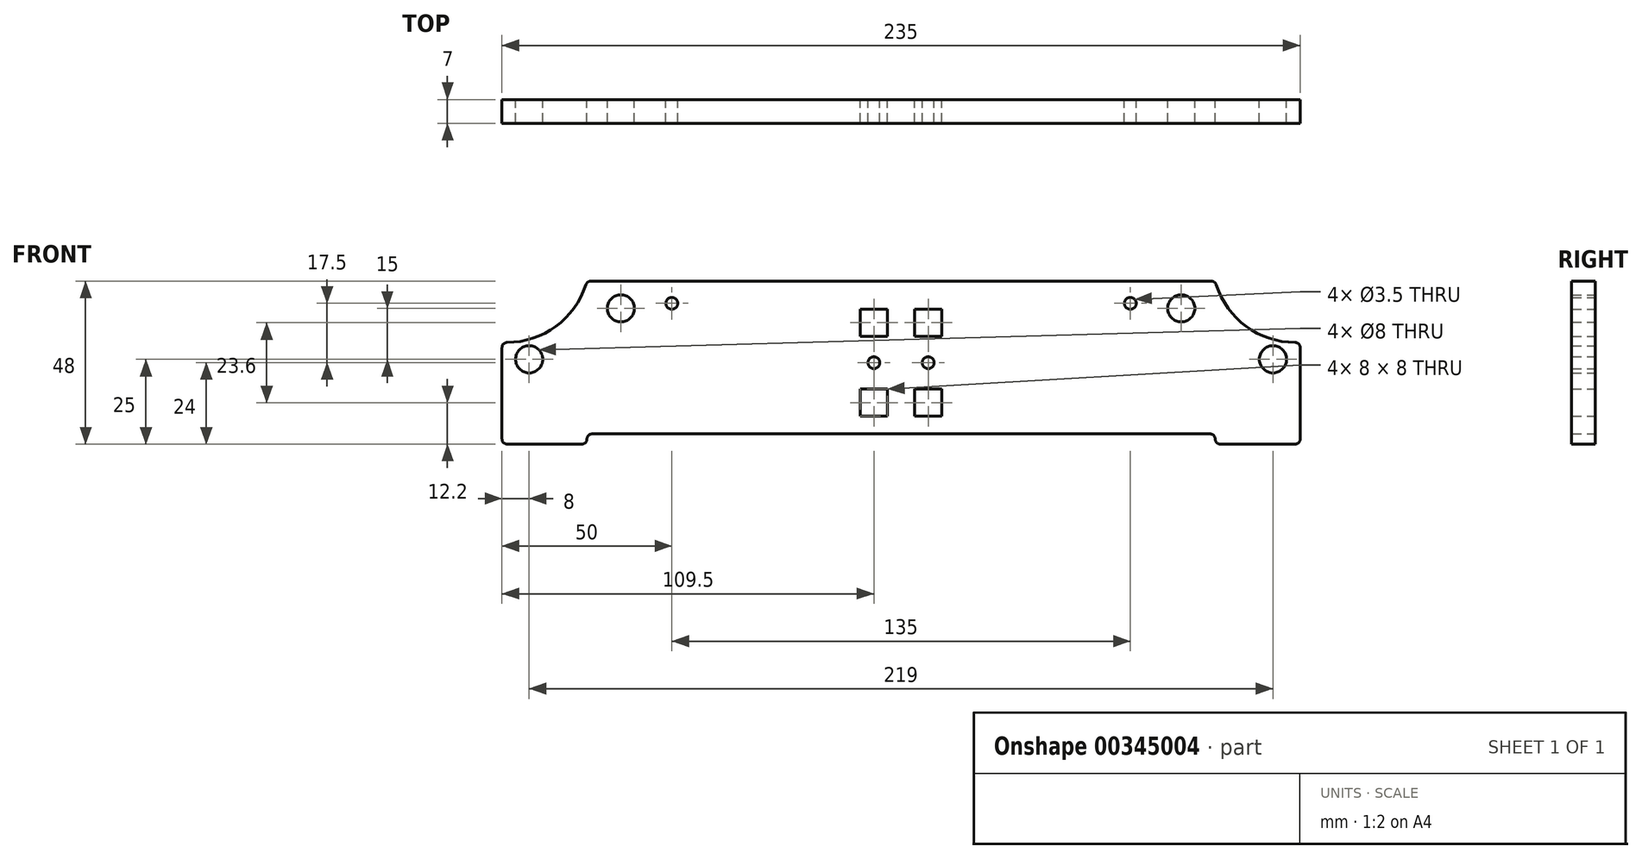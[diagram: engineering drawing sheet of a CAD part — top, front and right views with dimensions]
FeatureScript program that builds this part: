
annotation { "Feature Type Name" : "Feature", "Feature Type Description" : "" }
export const myFeature = defineFeature(function(context is Context, id is Id, definition is map)
    precondition{}
    {
        {
            var Q0;
            Q0=qCreatedBy(makeId("Front.planeOp"),FACE);
            var sketch = newSketch(context, id + "F0", { "sketchPlane" : qUnion([Q0])});
            skLineSegment(sketch, "E0", {"start": v(-117.5, 0) * mm, "end": v(117.5, 0) * mm, "construction": true});
            skLineSegment(sketch, "E1", {"start": v(0, 24) * mm, "end": v(0, -24) * mm, "construction": true});
            skPoint(sketch, "E2", {"position": v(-92.5, 0) * mm});
            skPoint(sketch, "E3.MirrorP", {"position": v(92.5, 0) * mm});
            skPoint(sketch, "E4", {"position": v(0, 21) * mm});
            skPoint(sketch, "E5.MirrorP", {"position": v(0, -21) * mm});
            skSolve(sketch);
        }
        {
            var Q0;
            Q0=qCreatedBy(makeId("Front.planeOp"),FACE);
            var sketch = newSketch(context, id + "F1", { "sketchPlane" : qUnion([Q0])});
            skLineSegment(sketch, "E6.0", {"start": v(-117.5, 0) * mm, "end": v(117.5, 0) * mm, "construction": true});
            skLineSegment(sketch, "E6.1", {"start": v(0, 24) * mm, "end": v(0, -24) * mm, "construction": true});
            skLineSegment(sketch, "E7", {"start": v(-91, -21) * mm, "end": v(92.5, -21) * mm});
            skLineSegment(sketch, "E8", {"start": v(-116, -24) * mm, "end": v(-94, -24) * mm});
            skLineSegment(sketch, "E9", {"start": v(-92.5, -22.5) * mm, "end": v(-92.5, -22.5) * mm});
            skPoint(sketch, "E10.visualSharp", {"position": v(-92.5, -24) * mm});
            skArc(sketch, "E10.filletArc", {"start": v(-94, -24) * mm, "mid": v(-92.94, -23.56) * mm, "end": v(-92.5, -22.5) * mm});
            skPoint(sketch, "E11.visualSharp", {"position": v(-92.5, -21) * mm});
            skArc(sketch, "E11.filletArc", {"start": v(-91, -21) * mm, "mid": v(-92.06, -21.44) * mm, "end": v(-92.5, -22.5) * mm});
            skArc(sketch, "E12.MirrorCS", {"start": v(-94, -24) * mm, "mid": v(-92.94, -24.44) * mm, "end": v(-92.5, -25.5) * mm});
            skArc(sketch, "E13.MirrorCS", {"start": v(-91, -27) * mm, "mid": v(-92.06, -26.56) * mm, "end": v(-92.5, -25.5) * mm});
            skPoint(sketch, "E14.MirrorP", {"position": v(-92.5, -27) * mm});
            skArc(sketch, "E15.MirrorCS", {"start": v(94, -24) * mm, "mid": v(92.94, -23.56) * mm, "end": v(92.5, -22.5) * mm});
            skArc(sketch, "E16.MirrorCS", {"start": v(94, -24) * mm, "mid": v(92.94, -24.44) * mm, "end": v(92.5, -25.5) * mm});
            skArc(sketch, "E17.MirrorCS", {"start": v(91, -21) * mm, "mid": v(92.06, -21.44) * mm, "end": v(92.5, -22.5) * mm});
            skArc(sketch, "E18.MirrorCS", {"start": v(91, -27) * mm, "mid": v(92.06, -26.56) * mm, "end": v(92.5, -25.5) * mm});
            skPoint(sketch, "E19.MirrorP", {"position": v(92.5, -24) * mm});
            skPoint(sketch, "E20.MirrorP", {"position": v(92.5, -21) * mm});
            skLineSegment(sketch, "E21.MirrorCS", {"start": v(92.5, -22.5) * mm, "end": v(92.5, -22.5) * mm});
            skPoint(sketch, "E22.MirrorP", {"position": v(92.5, -27) * mm});
            skLineSegment(sketch, "E23.MirrorCS", {"start": v(116, -24) * mm, "end": v(94, -24) * mm});
            skLineSegment(sketch, "E24", {"start": v(-91.38, 24) * mm, "end": v(92.5, 24) * mm});
            skLineSegment(sketch, "E25", {"start": v(-117.5, -22.5) * mm, "end": v(-117.5, 4.46) * mm});
            skLineSegment(sketch, "E26.MirrorCS", {"start": v(117.5, -22.5) * mm, "end": v(117.5, 6) * mm});
            skArc(sketch, "E27", {"start": v(-116, 5.96) * mm, "mid": v(-101.65, 10.7) * mm, "end": v(-92.8, 22.96) * mm});
            skPoint(sketch, "E28.visualSharp", {"position": v(-92.5, 24) * mm});
            skArc(sketch, "E28.filletArc", {"start": v(-91.38, 24) * mm, "mid": v(-92.26, 23.71) * mm, "end": v(-92.8, 22.96) * mm});
            skPoint(sketch, "E29.visualSharp", {"position": v(-117.5, 6) * mm});
            skArc(sketch, "E29.filletArc", {"start": v(-116, 5.96) * mm, "mid": v(-117.06, 5.52) * mm, "end": v(-117.5, 4.46) * mm});
            skArc(sketch, "E30.MirrorCS", {"start": v(116, 5.96) * mm, "mid": v(101.65, 10.7) * mm, "end": v(92.8, 22.96) * mm});
            skPoint(sketch, "E31.MirrorP", {"position": v(92.5, 24) * mm});
            skArc(sketch, "E32.MirrorCS", {"start": v(91.38, 24) * mm, "mid": v(92.26, 23.71) * mm, "end": v(92.8, 22.96) * mm});
            skArc(sketch, "E33.MirrorCS", {"start": v(116, 5.96) * mm, "mid": v(117.06, 5.52) * mm, "end": v(117.5, 4.46) * mm});
            skPoint(sketch, "E34.visualSharp", {"position": v(-117.5, -24) * mm});
            skArc(sketch, "E34.filletArc", {"start": v(-117.5, -22.5) * mm, "mid": v(-117.06, -23.56) * mm, "end": v(-116, -24) * mm});
            skPoint(sketch, "E35.visualSharp", {"position": v(117.5, -24) * mm});
            skArc(sketch, "E35.filletArc", {"start": v(116, -24) * mm, "mid": v(117.06, -23.56) * mm, "end": v(117.5, -22.5) * mm});
            skLineSegment(sketch, "E36.bottom", {"start": v(-4, -7.8) * mm, "end": v(-12, -7.8) * mm});
            skLineSegment(sketch, "E36.top", {"start": v(-4, -15.8) * mm, "end": v(-12, -15.8) * mm});
            skLineSegment(sketch, "E36.left", {"start": v(-4, -7.8) * mm, "end": v(-4, -15.8) * mm});
            skLineSegment(sketch, "E36.right", {"start": v(-12, -7.8) * mm, "end": v(-12, -15.8) * mm});
            skLineSegment(sketch, "E37", {"start": v(-8, -15.8) * mm, "end": v(-8, 0) * mm, "construction": true});
            skPoint(sketch, "E37.startSnap0", {"position": v(-8, -15.8) * mm});
            skPoint(sketch, "E37.endSnap0", {"position": v(-8, -7.8) * mm});
            skLineSegment(sketch, "E38.MirrorCS", {"start": v(-4, 15.8) * mm, "end": v(-12, 15.8) * mm});
            skLineSegment(sketch, "E39.MirrorCS", {"start": v(-4, 7.8) * mm, "end": v(-4, 15.8) * mm});
            skLineSegment(sketch, "E40.MirrorCS", {"start": v(-4, 7.8) * mm, "end": v(-12, 7.8) * mm});
            skLineSegment(sketch, "E41.MirrorCS", {"start": v(-12, 7.8) * mm, "end": v(-12, 15.8) * mm});
            skLineSegment(sketch, "E42", {"start": v(-8, 7.8) * mm, "end": v(-8, -7.8) * mm, "construction": true});
            skCircle(sketch, "E43", {"center": v(-8, 0) * mm, "radius": 1.75 * mm});
            skCircle(sketch, "E44", {"center": v(-67.5, 17.5) * mm, "radius": 1.75 * mm});
            skCircle(sketch, "E45", {"center": v(-82.5, 16) * mm, "radius": 4 * mm});
            skCircle(sketch, "E46", {"center": v(-109.5, 1) * mm, "radius": 4 * mm});
            skLineSegment(sketch, "E47.MirrorCS", {"start": v(4, 7.8) * mm, "end": v(4, 15.8) * mm});
            skLineSegment(sketch, "E48.MirrorCS", {"start": v(4, 7.8) * mm, "end": v(12, 7.8) * mm});
            skLineSegment(sketch, "E49.MirrorCS", {"start": v(12, 7.8) * mm, "end": v(12, 15.8) * mm});
            skLineSegment(sketch, "E50.MirrorCS", {"start": v(4, 15.8) * mm, "end": v(12, 15.8) * mm});
            skCircle(sketch, "E51.MirrorC", {"center": v(8, 0) * mm, "radius": 1.75 * mm});
            skLineSegment(sketch, "E52.MirrorCS", {"start": v(4, -7.8) * mm, "end": v(12, -7.8) * mm});
            skLineSegment(sketch, "E53.MirrorCS", {"start": v(12, -7.8) * mm, "end": v(12, -15.8) * mm});
            skLineSegment(sketch, "E54.MirrorCS", {"start": v(4, -7.8) * mm, "end": v(4, -15.8) * mm});
            skLineSegment(sketch, "E55.MirrorCS", {"start": v(4, -15.8) * mm, "end": v(12, -15.8) * mm});
            skCircle(sketch, "E56.MirrorC", {"center": v(67.5, 17.5) * mm, "radius": 1.75 * mm});
            skCircle(sketch, "E57.MirrorC", {"center": v(82.5, 16) * mm, "radius": 4 * mm});
            skCircle(sketch, "E58.MirrorC", {"center": v(109.5, 1) * mm, "radius": 4 * mm});
            skSolve(sketch);
        }
        {
            var Q0;
            Q0 = qSketchRegion(id + "F1", true);
            extrude(context, id + "F2", {"entities" : qUnion([Q0]), "endBound" : BoundingType.SYMMETRIC, "depth" : 7 * mm});
        }
    });
